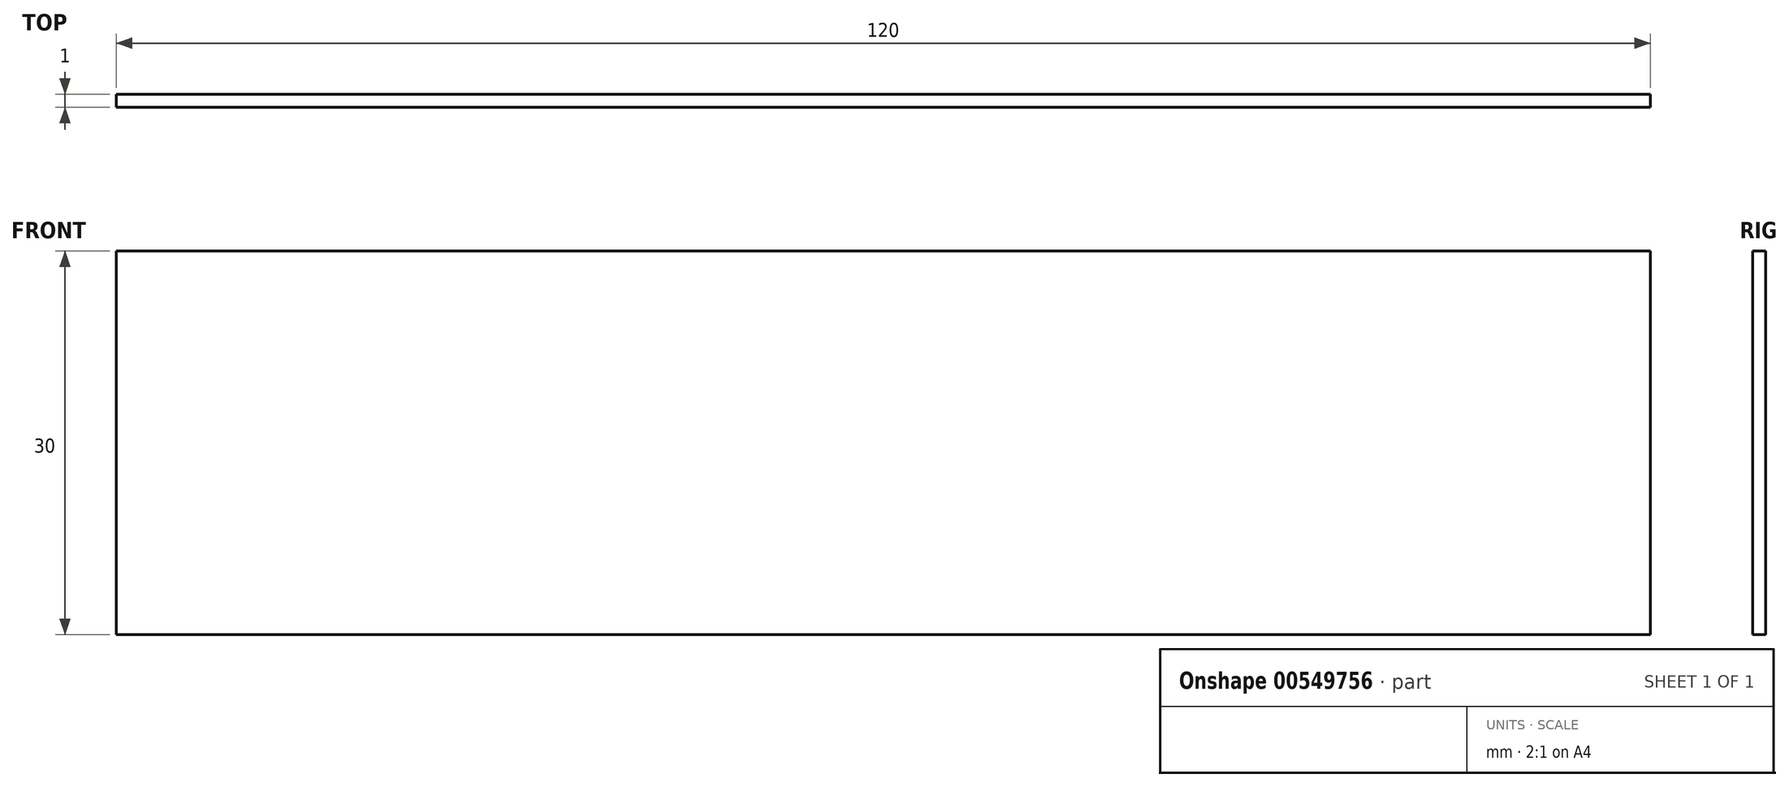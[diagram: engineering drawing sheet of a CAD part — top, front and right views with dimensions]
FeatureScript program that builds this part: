
annotation { "Feature Type Name" : "Feature", "Feature Type Description" : "" }
export const myFeature = defineFeature(function(context is Context, id is Id, definition is map)
    precondition{}
    {
        {
            var Q0;
            Q0=qCreatedBy(makeId("Front.planeOp"),FACE);
            var sketch = newSketch(context, id + "F0", { "sketchPlane" : qUnion([Q0])});
            skLineSegment(sketch, "E0.bottom", {"start": v(0, 0) * mm, "end": v(120, 0) * mm});
            skLineSegment(sketch, "E0.top", {"start": v(0, 30) * mm, "end": v(120, 30) * mm});
            skLineSegment(sketch, "E0.left", {"start": v(0, 0) * mm, "end": v(0, 30) * mm});
            skLineSegment(sketch, "E0.right", {"start": v(120, 0) * mm, "end": v(120, 30) * mm});
            skSolve(sketch);
        }
        {
            var Q0;
            Q0=makeQuery(id+"F0.imprint","IMPRINT",FACE,{"disambiguationData":[TD([[makeQuery(id+"F0.imprint","IMPRINT",EDGE,{"derivedFrom":sQuery(id+"F0.wireOp",EDGE,"E0.bottom")}),1.0]])]});
            extrude(context, id + "F1", {"entities" : qUnion([Q0]), "depth" : 1 * mm, "offsetDistance" : 25 * mm});
        }
    });
